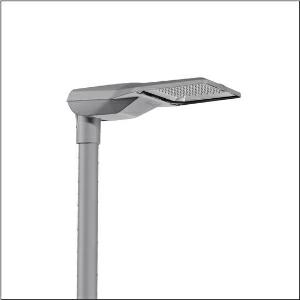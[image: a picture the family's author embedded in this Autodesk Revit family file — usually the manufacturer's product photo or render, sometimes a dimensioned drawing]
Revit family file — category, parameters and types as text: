
# Revit family: streetlight_sl_21_midi___st0_5a_5xe7b33a08mb_315d
name_source: partatom
category: Lighting Fixtures
units: mm (PartAtom-declared; Revit-internal decimal feet)

## family parameters
Cut with Voids When Loaded = No
Host = Face
Light Source = No
Part Type = Normal
Room Calculation Point = No
Round Connector Dimension = Use Diameter
Shared = No

## types (1)
- --- (1 x LED, 18270 lm, 136 W, 3000K)
    Apparent Load = 136 VA
    CIE Flux Codes = 41 75 97 100 100
    Color Rendering = 70
    Color Temperature = 3000K
    Default Elevation = 1800 mm
    Description = Streetlight SL 21 midi, mast luminaire, primary light control with lens, of PMMA, primary optical cover: cover, of toughened safety glass, transparent, light distribution: ST0.5a, light emission: direct distribution, primary light characteristic: asymmetric, installation type: post-top, side-entry, LED, 3G 1.5mm², High Power LED, rated luminous flux: 18.270lm, luminous efficacy: 134lm/W, light colour: 730, colour temperature: 3000K, control: overheat protection, constant luminous flux control, time-dependent luminous flux control, flexible luminous flux parameterisation, mains connection: 220..240V, AC, 50/60Hz, connection cable pre-assembled, cable length: 12,5m, wiring characteristics: H07RN-F, start of lifetime: 136W, end of service life: 142W, reduction: 61W, luminaire housing, of diecast aluminium, powder-coated, Siteco® metallic grey (DB 702S), corrosivity category C5 mid according to DIN EN ISO 12944, please order mast flange separately, inclination adjustable: 0°, 5°, 10°, 15°, sealing non-destructively replaceable, multi-level sealing system, length: 644mm, width: 335mm, height: 110mm, mast flange for spigot size: 42mm (side-entry): 5XC10008XM4, 60/48mm (side-entry/post-top): 5XC10108XM2, 76/60mm (side-entry/post-top): 5XC10108XM1, protection rating (complete): IP66, insulation class (complete): insulation class II (safety insulation), certification: CE, ENEC, ENEC+, VDE, impact resistance: IK09, permissible operating ambient temperature for outdoor applications: -40..+50°C, standard-compliant lighting for roads and squares, packaging unit: 1 piece

Light Distribution: ST0.5a
    Height = 111 mm
    Lamp = 1 x LED
    Lamp Light Flux = 18270 lm
    Lamp Power = 136 W
    Lamp count = 1
    Length = 644 mm
    Luminous efficacy = 134 lm/W
    Manufacturer = Siteco
    ModVariant = No
    Model = 5XE7B33A08MB
    Number of Poles = 1
    OnlyDefault = Yes
    Power Factor = 1
    Product Name = Streetlight SL 21 midi | ST0.5a
    Product group = mast luminaire | pylon top
    ProductGroupID = 6100
    Protection Class = Protection class II
    Protection Degree = IP 66
    RLX_Detail_Level = 1
    RLX_Emergency_Light_Flux = 0 lm
    RLX_Emergency_Type = 0
    RLX_Emergency_Type_DB = No
    RlxData = <blob elided: 101677 chars, md5=7338b500>
    Socket = socket
    Standby Power = 0 W
    System Light Flux = 18270 lm
    System Power = 136 W
    Type Comments = factory setting: luminous flux: 100 % | Output Level: 100 % | 695 mA
    Type Image = l_1004298.jpg
    URL = http://relux.com
    VarID = @adj_125633
    Voltage = 0 V
    Weight = 0.00 kg
    Width = 336 mm

## geometry (parser evidence)
native form markers: Blend x4, Sweep x10
no freeform markers — native parametric forms only
